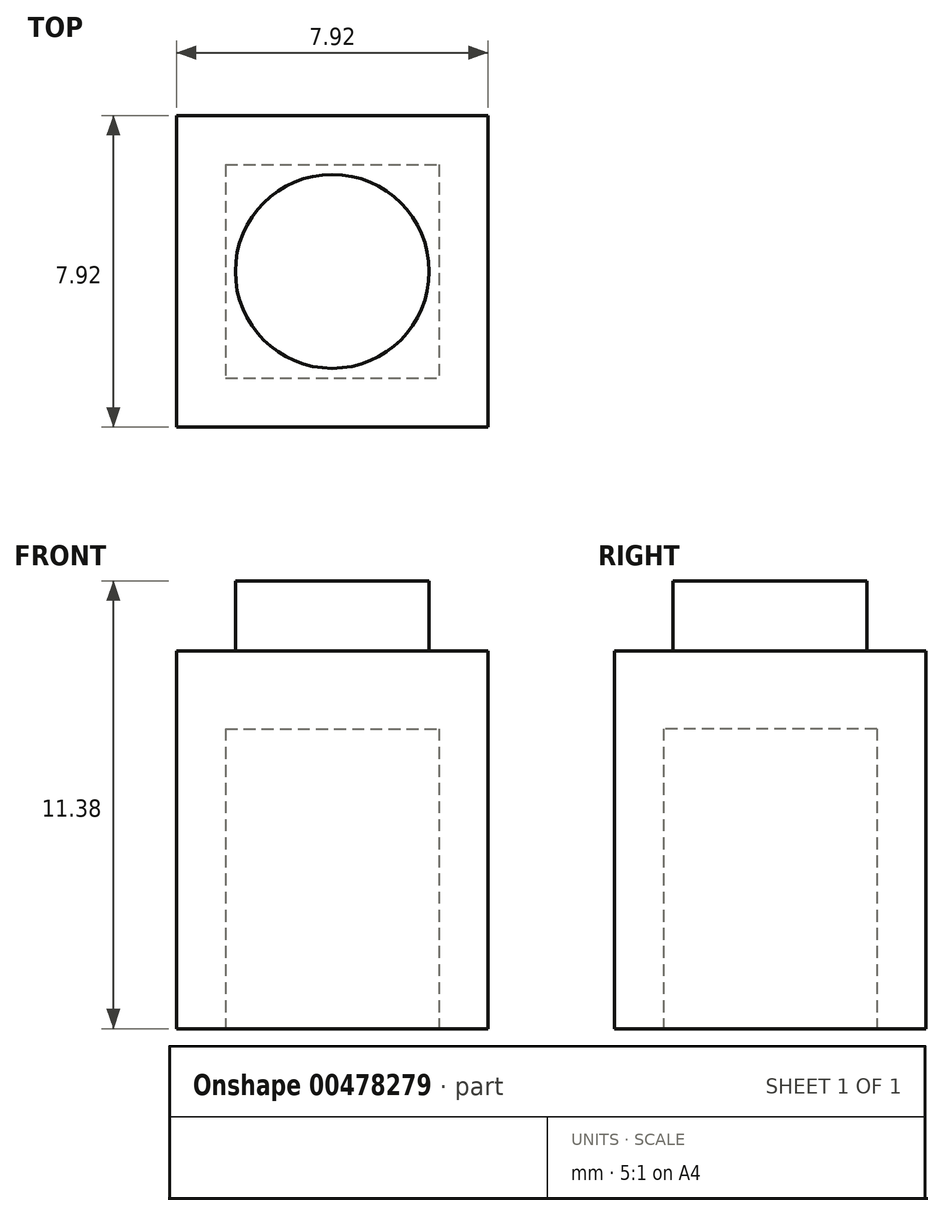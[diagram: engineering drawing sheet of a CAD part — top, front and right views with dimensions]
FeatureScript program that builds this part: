
annotation { "Feature Type Name" : "Feature", "Feature Type Description" : "" }
export const myFeature = defineFeature(function(context is Context, id is Id, definition is map)
    precondition{}
    {
        {
            var Q0;
            Q0=qCreatedBy(makeId("Top.planeOp"),FACE);
            var sketch = newSketch(context, id + "F0", { "sketchPlane" : qUnion([Q0])});
            skLineSegment(sketch, "E0.bottom", {"start": v(3.96, -3.96) * mm, "end": v(-3.96, -3.96) * mm});
            skLineSegment(sketch, "E0.top", {"start": v(3.96, 3.96) * mm, "end": v(-3.96, 3.96) * mm});
            skLineSegment(sketch, "E0.left", {"start": v(3.96, -3.96) * mm, "end": v(3.96, 3.96) * mm});
            skLineSegment(sketch, "E0.right", {"start": v(-3.96, -3.96) * mm, "end": v(-3.96, 3.96) * mm});
            skPoint(sketch, "E0.middle", {"position": v(0, 0) * mm});
            skSolve(sketch);
        }
        {
            var Q0;
            Q0=makeQuery(id+"F0.imprint","IMPRINT",FACE,{"disambiguationData":[TD([[makeQuery(id+"F0.imprint","IMPRINT",EDGE,{"derivedFrom":sQuery(id+"F0.wireOp",EDGE,"E0.bottom")}),-1.0]])]});
            var sketch = newSketch(context, id + "F1", { "sketchPlane" : qUnion([Q0])});
            skCircle(sketch, "E1", {"center": v(0, 0) * mm, "radius": 2.46 * mm});
            skSolve(sketch);
        }
        {
            var Q0;
            Q0=makeQuery(id+"F0.imprint","IMPRINT",FACE,{"disambiguationData":[TD([[makeQuery(id+"F0.imprint","IMPRINT",EDGE,{"derivedFrom":sQuery(id+"F0.wireOp",EDGE,"E0.bottom")}),-1.0]])]});
            extrude(context, id + "F2", {"entities" : qUnion([Q0]), "oppositeDirection" : true, "depth" : 9.6 * mm, "offsetDistance" : 25.4 * mm});
        }
        {
            var Q0;
            Q0=makeQuery(id+"F1.imprint","IMPRINT",FACE,{"disambiguationData":[TD([[makeQuery(id+"F1.imprint","IMPRINT",EDGE,{"derivedFrom":sQuery(id+"F1.wireOp",EDGE,"E1")}),1.0]])]});
            extrude(context, id + "F3", {"entities" : qUnion([Q0]), "operationType" : NewBodyOperationType.ADD, "depth" : 1.78 * mm, "offsetDistance" : 25.4 * mm});
        }
        {
            var Q0;
            Q0=makeQuery(id+"F2.opExtrude","CAP_FACE",FACE,{"disambiguationData":[OSD([sQuery(id+"F0.wireOp",EDGE,"E0.bottom"),sQuery(id+"F0.wireOp",EDGE,"E0.top"),sQuery(id+"F0.wireOp",EDGE,"E0.left"),sQuery(id+"F0.wireOp",EDGE,"E0.right")])],"isStart":false});
            var sketch = newSketch(context, id + "F4", { "sketchPlane" : qUnion([Q0])});
            skLineSegment(sketch, "E2.bottom", {"start": v(-2.71, -2.71) * mm, "end": v(2.71, -2.71) * mm});
            skLineSegment(sketch, "E2.top", {"start": v(-2.71, 2.71) * mm, "end": v(2.71, 2.71) * mm});
            skLineSegment(sketch, "E2.left", {"start": v(-2.71, -2.71) * mm, "end": v(-2.71, 2.71) * mm});
            skLineSegment(sketch, "E2.right", {"start": v(2.71, -2.71) * mm, "end": v(2.71, 2.71) * mm});
            skPoint(sketch, "E2.middle", {"position": v(0, 0) * mm});
            skSolve(sketch);
        }
        {
            var Q0;
            Q0=makeQuery(id+"F4.imprint","IMPRINT",FACE,{"disambiguationData":[TD([[makeQuery(id+"F4.imprint","IMPRINT",EDGE,{"derivedFrom":sQuery(id+"F4.wireOp",EDGE,"E2.bottom")}),1.0]])]});
            extrude(context, id + "F5", {"entities" : qUnion([Q0]), "operationType" : NewBodyOperationType.REMOVE, "oppositeDirection" : true, "depth" : 7.62 * mm, "offsetDistance" : 25.4 * mm});
        }
    });
